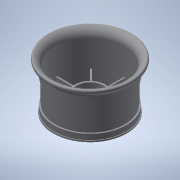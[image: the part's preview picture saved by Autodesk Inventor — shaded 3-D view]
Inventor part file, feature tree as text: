
AUTODESK INVENTOR PART (.ipt)
format: ipt  version: 2020 (Build 240168000, 168)  size: 318,976 bytes
history: native  units: mm
features: sketch x12, extrude x9, other x4, fillet x2, pattern_circular x1, projected_geometry x1
ambient origin geometry x8: Origin, YZ Plane, XZ Plane, XY Plane, X Axis, Y Axis, Z Axis, Center Point
bodies: Body1 (feature_tree)
feature tree (29):
  other  "實體1"
  extrude  "擠出1"  Depth=53.0mm
  extrude  "擠出2"  Depth=35.5mm TaperAngle=0.0deg
  other  "迴轉1"
  extrude  "擠出3"  Depth=61.3mm
  other  "迴轉2"
  extrude  "擠出4"  Depth=7.0mm TaperAngle=0.0deg
  fillet  "圓角1"  [1 undecoded]
  fillet  "圓角2"  Radius=54.0mm
  extrude  "擠出5"  Depth=1.0mm TaperAngle=0.0deg
  other  "迴轉3"
  extrude  "擠出6"  Depth=4.0mm
  extrude  "擠出7"  Depth=3.0mm
  pattern_circular  "環形陣列1"  [2 undecoded]
  extrude  "擠出8"  TaperAngle=90.0deg  [1 undecoded]
  extrude  "擠出9"  Depth=14.7mm
  sketch  "草圖1"
  sketch  "草圖2"
  sketch  "草圖3"
  sketch  "草圖4"
  sketch  "草圖5"
  sketch  "草圖6"
  sketch  "草圖7"
  sketch  "草圖8"
  sketch  "草圖9"
  sketch  "草圖10"
  sketch  "草圖11"
  projected_geometry  "投影迴路1"
  sketch  "草圖12"
note: 4 required parameter values undecoded (feature->parameter linkage not recoverable at this tier; creation-order binding heuristic only, values carry confidence <= 0.55)
